# Revit family: puz-dhrmp80_140ka_60Hz
name_source: partatom
category: 機械設備
units: mm (PartAtom-declared; Revit-internal decimal feet)

## family parameters
OmniClass タイトル = Split System Air Conditioning Units
OmniClass 番号 = 23.75.10.24.21.27.27
パーツ タイプ = 標準
ロード時にボイドで切り取り = いいえ
丸型コネクタ寸法 = 直径を使用
作業面ベース = いいえ
共有 = いいえ
常に垂直 = はい
部屋計算ポイント = いいえ

## types (3) — shared parameters
Clearance Back = 150  [stored 0.492126 ft]
Clearance Front = 500  [stored 1.64042 ft]
Clearance Left = 15  [stored 0.0492126 ft]
Clearance Right = 15  [stored 0.0492126 ft]
Depth = 330  [stored 1.08268 ft]
Height = 1338  [stored 4.38976 ft]
IfcExportAs = IfcUnitaryEquipmentType
IfcExportType = AIRCONDITIONINGUNIT
OmniClassCode = 23-33 17 13 11
URL = https://www.mitsubishielectric.co.jp
Uniclass2015Code = Pr_70_65_03_84
Uniclass2015Title = Split coil remote air cooled condensing units
Uniclass2015Version = Systems v1.9
Width = 1050
アンカーボルト位置X = 600  [stored 1.9685 ft]
アンカーボルト位置Y = 370  [stored 1.21391 ft]
サービススペース = はい
ドレン　位置X = 45  [stored 0.147638 ft]
ドレン　位置Y = 176  [stored 0.577428 ft]
ドレン　位置Z = 23  [stored 0.0754593 ft]
ドレン管径 = 33.00 mm
ユニット数 = 1
仕様書バージョン = Version1.0
企業コード = 108420
冷媒ガス管径 = 15.88 mm
冷媒液管径 = 9.52 mm
冷媒管位置X = 453  [stored 1.48622 ft]
冷媒管位置Y = 262  [stored 0.85958 ft]
冷媒管位置Z = 450  [stored 1.47638 ft]
冷媒管径 = 100.00 mm
冷媒管径符号 = Bd
冷媒管（ガス）位置X = 483
冷媒管（ガス）位置Y = 234  [stored 0.767717 ft]
冷媒管（液）位置X = 423  [stored 1.3878 ft]
冷媒管（液）位置Y = 290  [stored 0.951444 ft]
分類コード = 50053003126100
参照している仕様書等のバージョン = 公共建築物標準仕様書（機械設備工事編）平成31年度版
周波数 = 60 Hz
呼称 = パッケージ形空気調和機_室外機
始動方式 = インバータ始動方式
形名 = PUZ-ZRMP-3 : PUZ-ZRMP112KA11
形式 = パッケージ形 室外機
最大電流値 = 0 A
最小電線太さ_mm2 = 1.6
本体マテリアル = <カテゴリ別>
極数 = 3
法定耐用年数 = 6
発停方法 = 付属スイッチ
相 = 3
積算_科目 = 1 空気調和設備
符号 = PAC
製品リリース年月 = 2022/10/11
製品出荷対象 = 国内
製品質量 = 115.00 kg
製造元 = 三菱電機株式会社
設置方法 = 床置形
説明 = 空冷H/P PAC インバータ室外機
負荷分類 = 1_熱源類
質量 = 138.00 kg
運転方法 = 冷暖切替
運転質量 = 0.00 kg
電動機出力_送風機 = 0 kW
電圧 = 200 V
電源位置X = 325  [stored 1.06627 ft]
電源位置Y = 2  [stored 0.00656168 ft]
電源位置Z = 1063
zero-valued in all types: APF, COP, Clearance Bottom, Clearance Top, 据付ピッチ1

## per-type parameters (varying)
| type | 価格 | 冷房能力 | 推奨ブレーカー容量 | 暖房能力 | 消費電力 | 消費電力_冷房 | 消費電力_暖房 | 電動機出力_圧縮機 | 音響パワーレベル(dB) | 音響パワーレベル（冷）(dB) |
| PUZ-DHRMP80KA | 831000 $ | 7 kW | 30 A | 8 kW | 2 kW | 2 kW | 2 kW | 2 kW | 68 | 66 |
| PUZ-DHRMP112KA | 981000 $ | 10 kW | 30 A | 11 kW | 3 kW | 3 kW | 3 kW | 2 kW | 69 | 66 |
| PUZ-DHRMP140KA | 1171000 $ | 13 kW | 40 A | 14 kW | 4 kW | 4 kW | 4 kW | 3 kW | 69 | 68 |

note: column(s) folded — value = type name in every type: 構成品番

note: [stored X ft] marks values corroborated as IEEE doubles in the binary element streams (Revit-internal decimal feet)
